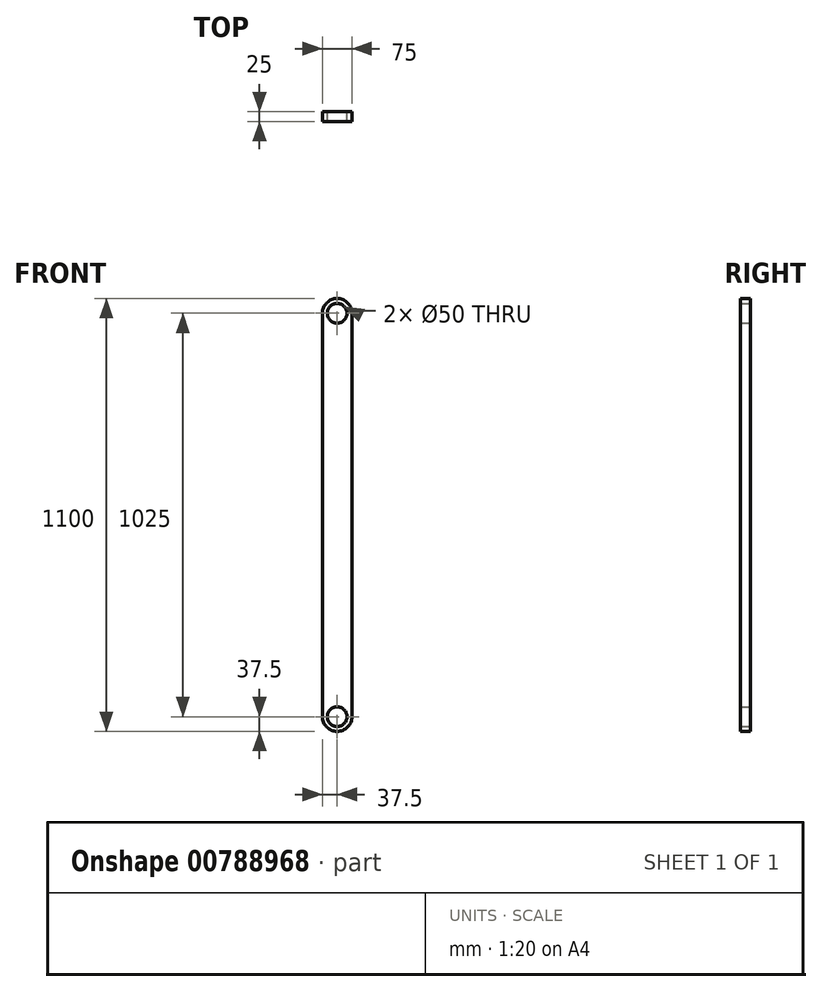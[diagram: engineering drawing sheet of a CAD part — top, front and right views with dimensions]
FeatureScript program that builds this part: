
annotation { "Feature Type Name" : "Feature", "Feature Type Description" : "" }
export const myFeature = defineFeature(function(context is Context, id is Id, definition is map)
    precondition{}
    {
        {
            var Q0;
            Q0=qCreatedBy(makeId("Front.planeOp"),FACE);
            var sketch = newSketch(context, id + "F0", { "sketchPlane" : qUnion([Q0])});
            skCircle(sketch, "E0", {"center": v(0, 0) * mm, "radius": 37.5 * mm});
            skLineSegment(sketch, "E1", {"start": v(-37.5, 0) * mm, "end": v(-37.5, 1025) * mm});
            skLineSegment(sketch, "E2", {"start": v(37.5, 0) * mm, "end": v(37.5, 1025) * mm});
            skLineSegment(sketch, "E3", {"start": v(-37.5, 1025) * mm, "end": v(37.5, 1025) * mm, "construction": true});
            skCircle(sketch, "E4", {"center": v(0, 0) * mm, "radius": 25 * mm});
            skCircle(sketch, "E5", {"center": v(0, 1025) * mm, "radius": 37.5 * mm});
            skCircle(sketch, "E6", {"center": v(0, 1025) * mm, "radius": 25 * mm});
            skSolve(sketch);
        }
        {
            var Q0;
            Q0=makeQuery(id+"F0.imprint","IMPRINT",FACE,{"disambiguationData":[TD([[makeQuery(id+"F0.imprint","IMPRINT",EDGE,{"derivedFrom":sQuery(id+"F0.wireOp",EDGE,"E4")}),-1.0]])]});
            var Q1;
            Q1=makeQuery(id+"F0.imprint","IMPRINT",FACE,{"disambiguationData":[TD([[makeQuery(id+"F0.imprint","IMPRINT",EDGE,{"derivedFrom":sQuery(id+"F0.wireOp",EDGE,"E6")}),-1.0]])]});
            var Q2;
            {var subQ0=sQuery(id+"F0.wireOp",EDGE,"E1");Q2=makeQuery(id+"F0.imprint","IMPRINT",FACE,{"disambiguationData":[TD([[makeQuery(id+"F0.imprint","IMPRINT",EDGE,{"derivedFrom":subQ0}),-1.0]])]});}
            extrude(context, id + "F1", {"entities" : qUnion([Q0, Q1, Q2]), "depth" : 25 * mm, "offsetDistance" : 25 * mm});
        }
    });
